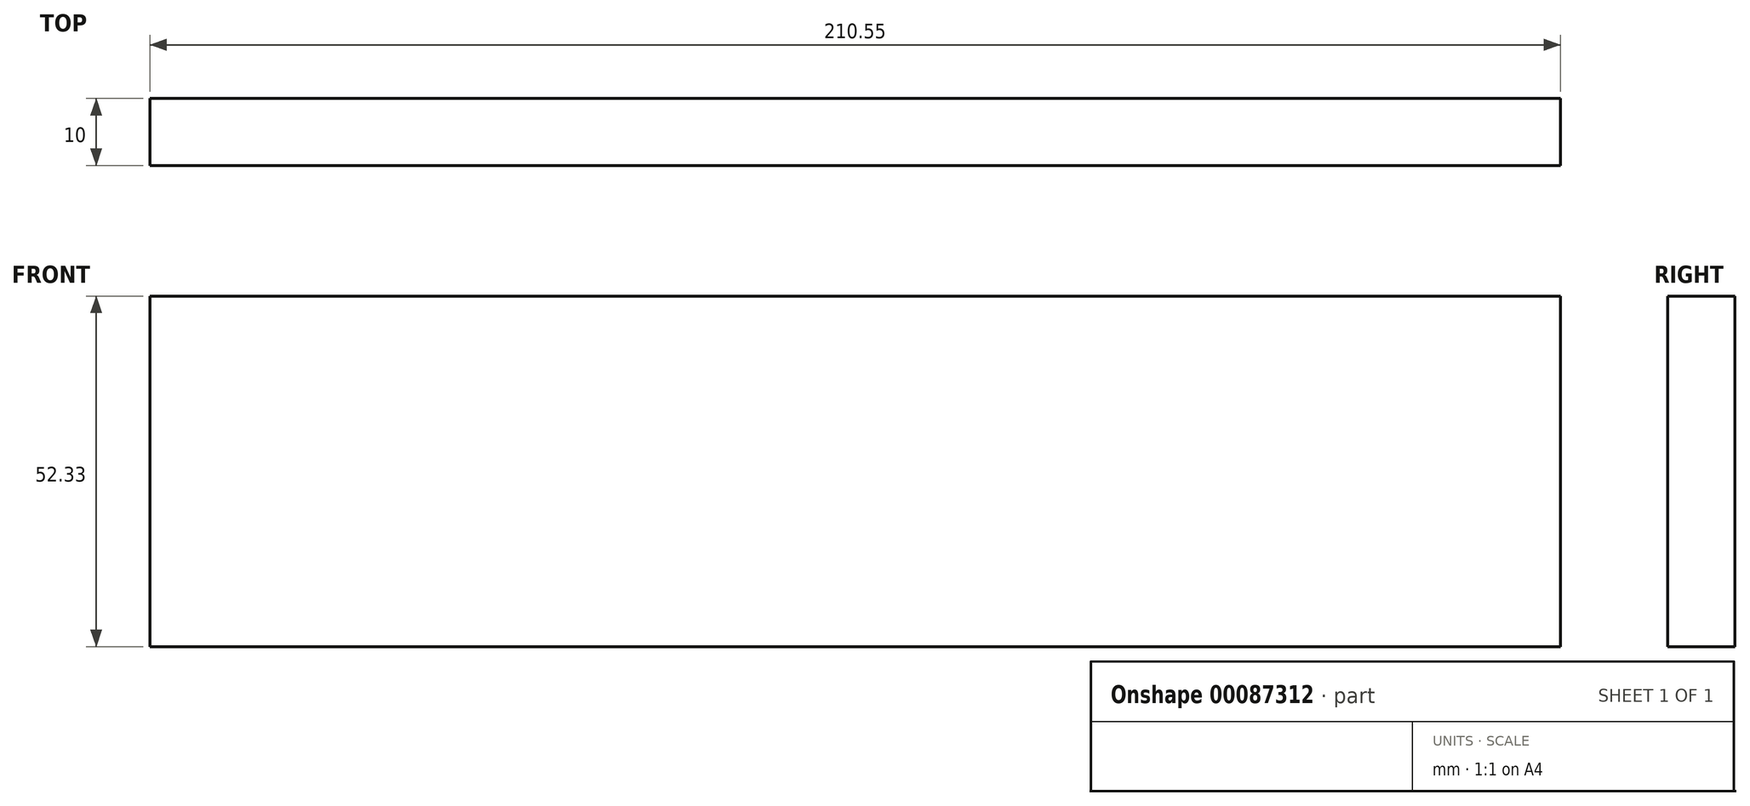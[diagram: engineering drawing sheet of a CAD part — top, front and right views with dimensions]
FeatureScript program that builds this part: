
annotation { "Feature Type Name" : "Feature", "Feature Type Description" : "" }
export const myFeature = defineFeature(function(context is Context, id is Id, definition is map)
    precondition{}
    {
        {
            var Q0;
            Q0=qCreatedBy(makeId("Front.planeOp"),FACE);
            var sketch = newSketch(context, id + "F0", { "sketchPlane" : qUnion([Q0])});
            skLineSegment(sketch, "E0.bottom", {"start": v(-135.4, 62.9) * mm, "end": v(155.15, 62.9) * mm});
            skLineSegment(sketch, "E0.top", {"start": v(-135.4, -69.42) * mm, "end": v(155.15, -69.42) * mm});
            skLineSegment(sketch, "E0.left", {"start": v(-135.4, 62.9) * mm, "end": v(-135.4, -69.42) * mm});
            skLineSegment(sketch, "E0.right", {"start": v(155.15, 62.9) * mm, "end": v(155.15, -69.42) * mm});
            skLineSegment(sketch, "E1.0", {"start": v(115.15, 22.9) * mm, "end": v(115.15, -29.42) * mm});
            skLineSegment(sketch, "E1.1", {"start": v(-95.4, 22.9) * mm, "end": v(115.15, 22.9) * mm});
            skLineSegment(sketch, "E1.2", {"start": v(-95.4, 22.9) * mm, "end": v(-95.4, -29.42) * mm});
            skLineSegment(sketch, "E1.3", {"start": v(-95.4, -29.42) * mm, "end": v(115.15, -29.42) * mm});
            skSolve(sketch);
        }
        {
            var Q0;
            Q0=makeQuery(id+"F0.imprint","IMPRINT",FACE,{"disambiguationData":[TD([[makeQuery(id+"F0.imprint","IMPRINT",EDGE,{"derivedFrom":sQuery(id+"F0.wireOp",EDGE,"E1.0")}),-1.0]])]});
            extrude(context, id + "F1", {"entities" : qUnion([Q0]), "depth" : 10 * mm});
        }
    });
